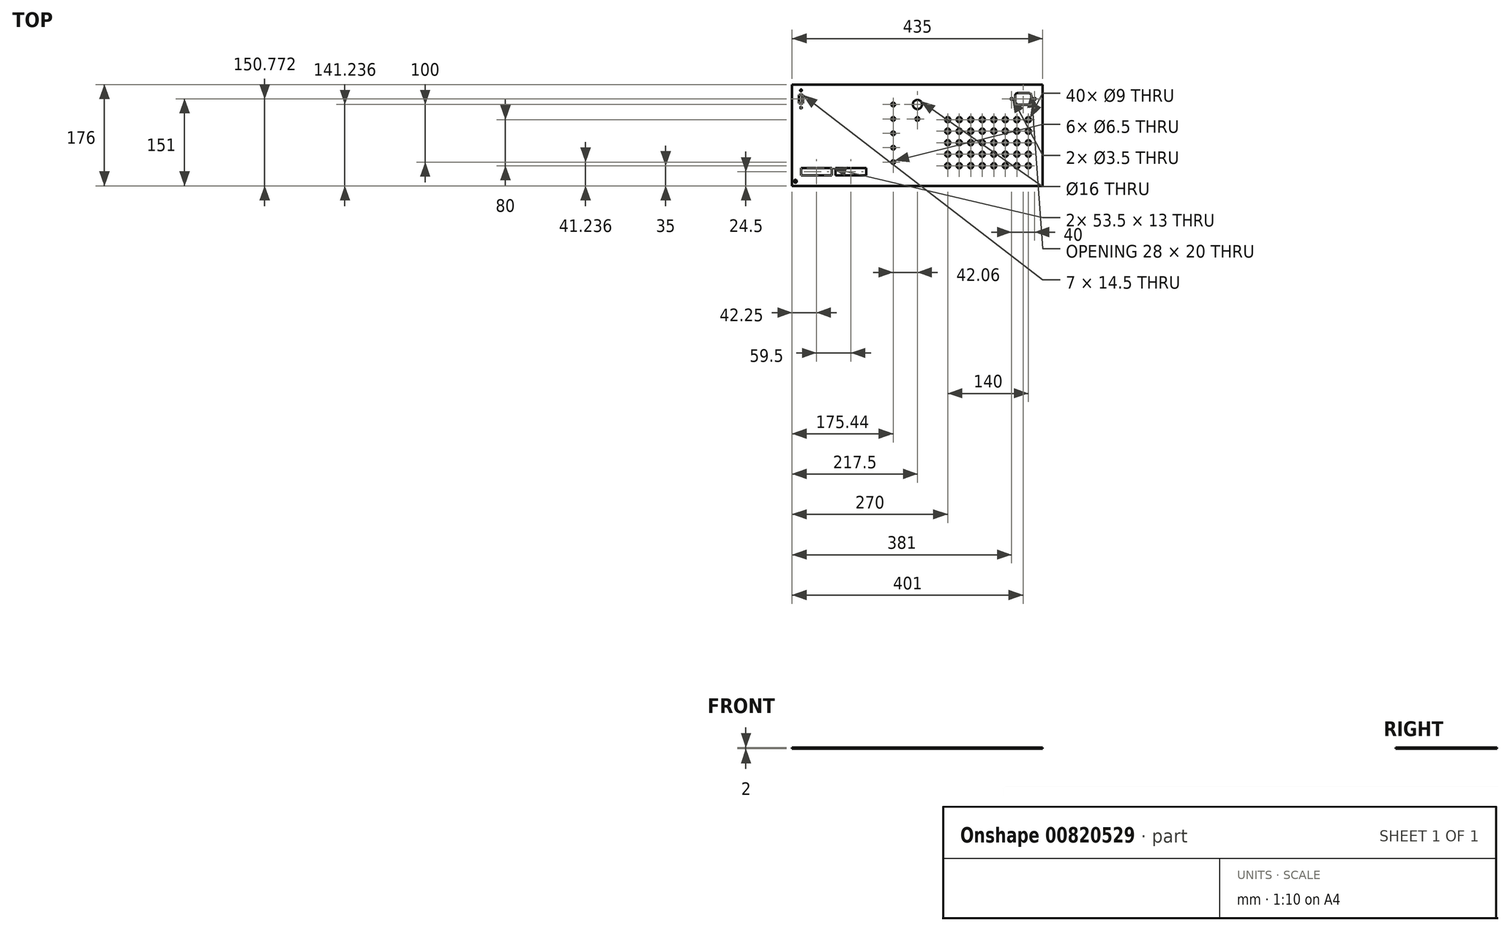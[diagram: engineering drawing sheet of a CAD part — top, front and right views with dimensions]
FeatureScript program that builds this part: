
annotation { "Feature Type Name" : "Feature", "Feature Type Description" : "" }
export const myFeature = defineFeature(function(context is Context, id is Id, definition is map)
    precondition{}
    {
        {
            var Q0;
            Q0=qCreatedBy(makeId("Top.planeOp"),FACE);
            var sketch = newSketch(context, id + "F0", { "sketchPlane" : qUnion([Q0])});
            skLineSegment(sketch, "E0.bottom", {"start": v(-217.5, 88) * mm, "end": v(217.5, 88) * mm});
            skLineSegment(sketch, "E0.top", {"start": v(-217.5, -88) * mm, "end": v(217.5, -88) * mm});
            skLineSegment(sketch, "E0.left", {"start": v(-217.5, 88) * mm, "end": v(-217.5, -88) * mm});
            skLineSegment(sketch, "E0.right", {"start": v(217.5, 88) * mm, "end": v(217.5, -88) * mm});
            skPoint(sketch, "E0.middle", {"position": v(0, 0) * mm});
            skCircle(sketch, "E1", {"center": v(192.5, -53) * mm, "radius": 4.5 * mm});
            skCircle(sketch, "E2.0.1.0", {"center": v(192.5, -33) * mm, "radius": 4.5 * mm});
            skCircle(sketch, "E2.0.2.0", {"center": v(192.5, -13) * mm, "radius": 4.5 * mm});
            skCircle(sketch, "E2.0.3.0", {"center": v(192.5, 7) * mm, "radius": 4.5 * mm});
            skCircle(sketch, "E2.0.4.0", {"center": v(192.5, 27) * mm, "radius": 4.5 * mm});
            skCircle(sketch, "E2.1.0.0", {"center": v(172.5, -53) * mm, "radius": 4.5 * mm});
            skCircle(sketch, "E2.1.1.0", {"center": v(172.5, -33) * mm, "radius": 4.5 * mm});
            skCircle(sketch, "E2.1.2.0", {"center": v(172.5, -13) * mm, "radius": 4.5 * mm});
            skCircle(sketch, "E2.1.3.0", {"center": v(172.5, 7) * mm, "radius": 4.5 * mm});
            skCircle(sketch, "E2.1.4.0", {"center": v(172.5, 27) * mm, "radius": 4.5 * mm});
            skCircle(sketch, "E2.2.0.0", {"center": v(152.5, -53) * mm, "radius": 4.5 * mm});
            skCircle(sketch, "E2.2.1.0", {"center": v(152.5, -33) * mm, "radius": 4.5 * mm});
            skCircle(sketch, "E2.2.2.0", {"center": v(152.5, -13) * mm, "radius": 4.5 * mm});
            skCircle(sketch, "E2.2.3.0", {"center": v(152.5, 7) * mm, "radius": 4.5 * mm});
            skCircle(sketch, "E2.2.4.0", {"center": v(152.5, 27) * mm, "radius": 4.5 * mm});
            skCircle(sketch, "E2.3.0.0", {"center": v(132.5, -53) * mm, "radius": 4.5 * mm});
            skCircle(sketch, "E2.3.1.0", {"center": v(132.5, -33) * mm, "radius": 4.5 * mm});
            skCircle(sketch, "E2.3.2.0", {"center": v(132.5, -13) * mm, "radius": 4.5 * mm});
            skCircle(sketch, "E2.3.3.0", {"center": v(132.5, 7) * mm, "radius": 4.5 * mm});
            skCircle(sketch, "E2.3.4.0", {"center": v(132.5, 27) * mm, "radius": 4.5 * mm});
            skCircle(sketch, "E2.4.0.0", {"center": v(112.5, -53) * mm, "radius": 4.5 * mm});
            skCircle(sketch, "E2.4.1.0", {"center": v(112.5, -33) * mm, "radius": 4.5 * mm});
            skCircle(sketch, "E2.4.2.0", {"center": v(112.5, -13) * mm, "radius": 4.5 * mm});
            skCircle(sketch, "E2.4.3.0", {"center": v(112.5, 7) * mm, "radius": 4.5 * mm});
            skCircle(sketch, "E2.4.4.0", {"center": v(112.5, 27) * mm, "radius": 4.5 * mm});
            skCircle(sketch, "E2.5.0.0", {"center": v(92.5, -53) * mm, "radius": 4.5 * mm});
            skCircle(sketch, "E2.5.1.0", {"center": v(92.5, -33) * mm, "radius": 4.5 * mm});
            skCircle(sketch, "E2.5.2.0", {"center": v(92.5, -13) * mm, "radius": 4.5 * mm});
            skCircle(sketch, "E2.5.3.0", {"center": v(92.5, 7) * mm, "radius": 4.5 * mm});
            skCircle(sketch, "E2.5.4.0", {"center": v(92.5, 27) * mm, "radius": 4.5 * mm});
            skCircle(sketch, "E2.6.0.0", {"center": v(72.5, -53) * mm, "radius": 4.5 * mm});
            skCircle(sketch, "E2.6.1.0", {"center": v(72.5, -33) * mm, "radius": 4.5 * mm});
            skCircle(sketch, "E2.6.2.0", {"center": v(72.5, -13) * mm, "radius": 4.5 * mm});
            skCircle(sketch, "E2.6.3.0", {"center": v(72.5, 7) * mm, "radius": 4.5 * mm});
            skCircle(sketch, "E2.6.4.0", {"center": v(72.5, 27) * mm, "radius": 4.5 * mm});
            skCircle(sketch, "E2.7.0.0", {"center": v(52.5, -53) * mm, "radius": 4.5 * mm});
            skCircle(sketch, "E2.7.1.0", {"center": v(52.5, -33) * mm, "radius": 4.5 * mm});
            skCircle(sketch, "E2.7.2.0", {"center": v(52.5, -13) * mm, "radius": 4.5 * mm});
            skCircle(sketch, "E2.7.3.0", {"center": v(52.5, 7) * mm, "radius": 4.5 * mm});
            skCircle(sketch, "E2.7.4.0", {"center": v(52.5, 27) * mm, "radius": 4.5 * mm});
            skLineSegment(sketch, "E2.direction1", {"start": v(192.5, -53) * mm, "end": v(172.5, -53) * mm, "construction": true});
            skLineSegment(sketch, "E2.direction2", {"start": v(192.5, -53) * mm, "end": v(192.5, -33) * mm, "construction": true});
            skLineSegment(sketch, "E3.bottom", {"start": v(-198.5, 55.52) * mm, "end": v(-205.5, 55.52) * mm});
            skLineSegment(sketch, "E3.top", {"start": v(-198.5, 70.02) * mm, "end": v(-205.5, 70.02) * mm});
            skLineSegment(sketch, "E3.left", {"start": v(-198.5, 55.52) * mm, "end": v(-198.5, 70.02) * mm});
            skLineSegment(sketch, "E3.right", {"start": v(-205.5, 55.52) * mm, "end": v(-205.5, 70.02) * mm});
            skPoint(sketch, "E3.middle", {"position": v(-202, 62.77) * mm});
            skCircle(sketch, "E4", {"center": v(-202, 77.82) * mm, "radius": 1.5 * mm});
            skCircle(sketch, "E5", {"center": v(-202, 47.72) * mm, "radius": 1.5 * mm});
            skLineSegment(sketch, "E6.bottom", {"start": v(193.5, 53) * mm, "end": v(173.5, 53) * mm});
            skLineSegment(sketch, "E6.top", {"start": v(193.5, 73) * mm, "end": v(173.5, 73) * mm});
            skLineSegment(sketch, "E6.left", {"start": v(197.5, 57) * mm, "end": v(197.5, 69) * mm});
            skLineSegment(sketch, "E6.right", {"start": v(169.5, 57) * mm, "end": v(169.5, 69) * mm});
            skPoint(sketch, "E6.middle", {"position": v(183.5, 63) * mm});
            skCircle(sketch, "E7", {"center": v(163.5, 63) * mm, "radius": 1.75 * mm});
            skCircle(sketch, "E8", {"center": v(203.5, 63) * mm, "radius": 1.75 * mm});
            skCircle(sketch, "E9", {"center": v(-42.06, 53.24) * mm, "radius": 3.25 * mm});
            skCircle(sketch, "E10", {"center": v(0, 28.24) * mm, "radius": 3.25 * mm});
            skCircle(sketch, "E11", {"center": v(0, 53.24) * mm, "radius": 8 * mm});
            skCircle(sketch, "E12.7.4.0", {"center": v(-211.72, -80) * mm, "radius": 2.5 * mm});
            skLineSegment(sketch, "E13.bottom", {"start": v(-148.5, -70) * mm, "end": v(-202, -70) * mm});
            skLineSegment(sketch, "E13.top", {"start": v(-148.5, -57) * mm, "end": v(-202, -57) * mm});
            skLineSegment(sketch, "E13.left", {"start": v(-148.5, -70) * mm, "end": v(-148.5, -57) * mm});
            skLineSegment(sketch, "E13.right", {"start": v(-202, -70) * mm, "end": v(-202, -57) * mm});
            skPoint(sketch, "E13.middle", {"position": v(-175.25, -63.5) * mm});
            skLineSegment(sketch, "E14.bottom", {"start": v(-89, -70) * mm, "end": v(-142.5, -70) * mm});
            skLineSegment(sketch, "E14.top", {"start": v(-89, -57) * mm, "end": v(-142.5, -57) * mm});
            skLineSegment(sketch, "E14.left", {"start": v(-89, -70) * mm, "end": v(-89, -57) * mm});
            skLineSegment(sketch, "E14.right", {"start": v(-142.5, -70) * mm, "end": v(-142.5, -57) * mm});
            skPoint(sketch, "E14.middle", {"position": v(-115.75, -63.5) * mm});
            skCircle(sketch, "E15.0.1.0", {"center": v(-42.06, 28.24) * mm, "radius": 3.25 * mm});
            skCircle(sketch, "E15.0.2.0", {"center": v(-42.06, 3.24) * mm, "radius": 3.25 * mm});
            skCircle(sketch, "E15.0.3.0", {"center": v(-42.06, -21.76) * mm, "radius": 3.25 * mm});
            skCircle(sketch, "E15.0.4.0", {"center": v(-42.06, -46.76) * mm, "radius": 3.25 * mm});
            skLineSegment(sketch, "E15.direction1", {"start": v(-42.06, 53.24) * mm, "end": v(-17.64, 53.24) * mm, "construction": true});
            skLineSegment(sketch, "E15.direction2", {"start": v(-42.06, 53.24) * mm, "end": v(-42.06, 28.24) * mm, "construction": true});
            skPoint(sketch, "E16.visualSharp", {"position": v(169.5, 73) * mm});
            skArc(sketch, "E16.filletArc", {"start": v(173.5, 73) * mm, "mid": v(170.67, 71.83) * mm, "end": v(169.5, 69) * mm});
            skPoint(sketch, "E17.visualSharp", {"position": v(197.5, 73) * mm});
            skArc(sketch, "E17.filletArc", {"start": v(197.5, 69) * mm, "mid": v(196.33, 71.83) * mm, "end": v(193.5, 73) * mm});
            skPoint(sketch, "E18.visualSharp", {"position": v(197.5, 53) * mm});
            skArc(sketch, "E18.filletArc", {"start": v(193.5, 53) * mm, "mid": v(196.33, 54.17) * mm, "end": v(197.5, 57) * mm});
            skPoint(sketch, "E19.visualSharp", {"position": v(169.5, 53) * mm});
            skArc(sketch, "E19.filletArc", {"start": v(169.5, 57) * mm, "mid": v(170.67, 54.17) * mm, "end": v(173.5, 53) * mm});
            skLineSegment(sketch, "E20", {"start": v(-205.5, 0) * mm, "end": v(-205.5, -80) * mm, "construction": true});
            skLineSegment(sketch, "E21", {"start": v(-205.5, -80) * mm, "end": v(-85.5, -80) * mm, "construction": true});
            skLineSegment(sketch, "E22", {"start": v(-85.5, -80) * mm, "end": v(-85.5, 0) * mm, "construction": true});
            skLineSegment(sketch, "E23", {"start": v(-85.5, 0) * mm, "end": v(-205.5, 0) * mm, "construction": true});
            skLineSegment(sketch, "E24", {"start": v(37.5, 42) * mm, "end": v(37.5, -68) * mm, "construction": true});
            skLineSegment(sketch, "E25", {"start": v(37.5, -68) * mm, "end": v(207.5, -68) * mm, "construction": true});
            skLineSegment(sketch, "E26", {"start": v(207.5, -68) * mm, "end": v(207.5, 42) * mm, "construction": true});
            skLineSegment(sketch, "E27", {"start": v(207.5, 42) * mm, "end": v(37.5, 42) * mm, "construction": true});
            skSolve(sketch);
        }
        {
            var Q0;
            Q0=qSketchRegion(id+"F0",true);
            extrude(context, id + "F1", {"entities" : qUnion([Q0]), "oppositeDirection" : true, "depth" : 2 * mm});
        }
    });
